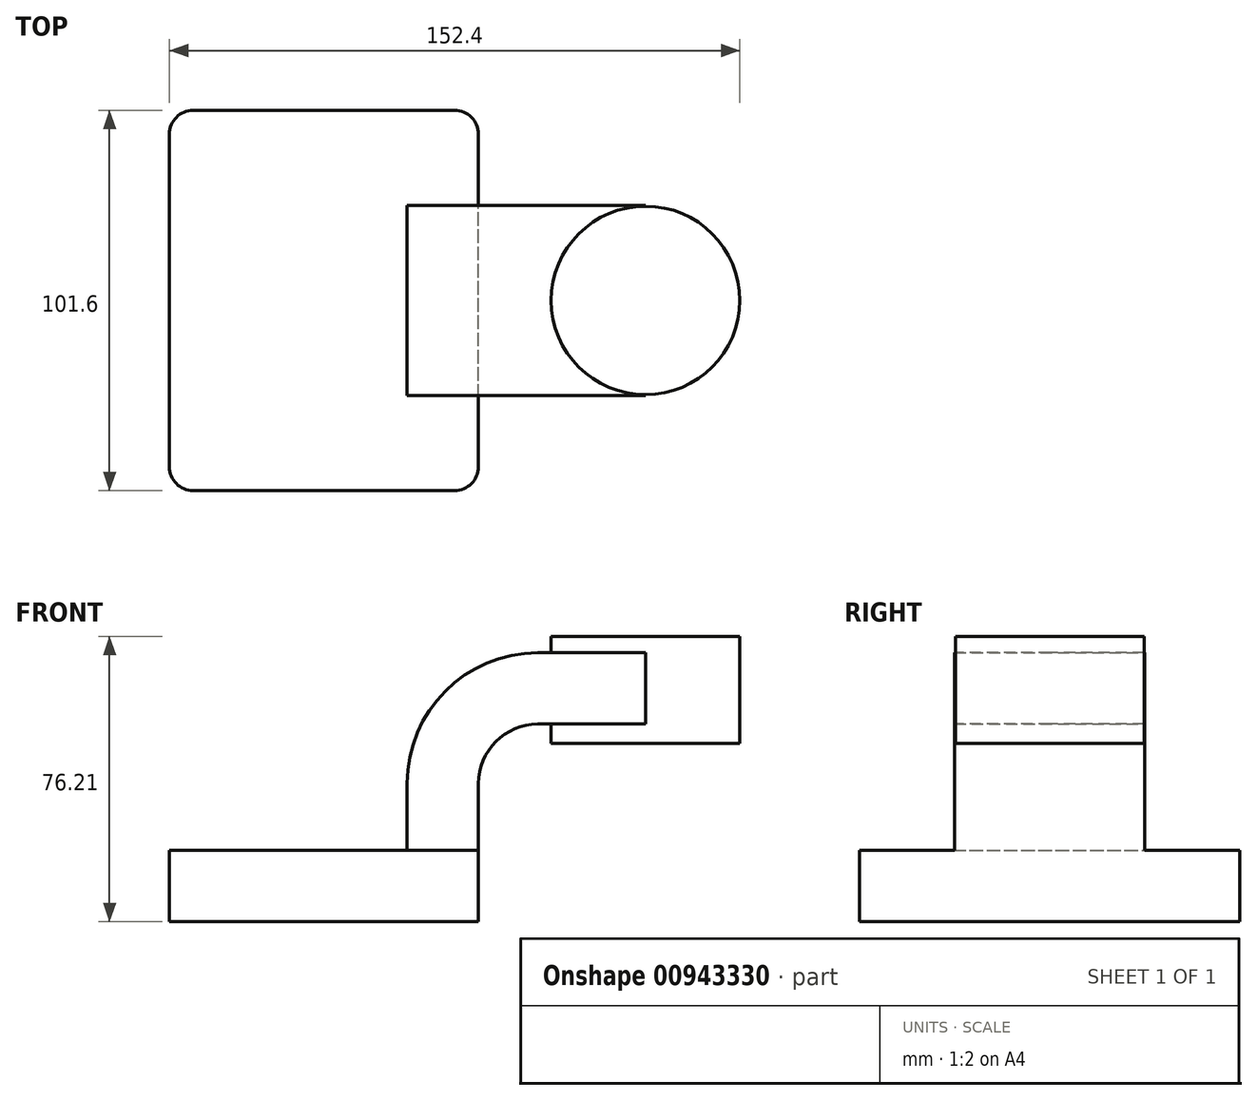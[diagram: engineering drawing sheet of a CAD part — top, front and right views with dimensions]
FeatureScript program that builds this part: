
annotation { "Feature Type Name" : "Feature", "Feature Type Description" : "" }
export const myFeature = defineFeature(function(context is Context, id is Id, definition is map)
    precondition{}
    {
        {
            var Q0;
            Q0=qCreatedBy(makeId("Front.planeOp"),FACE);
            var sketch = newSketch(context, id + "F0", { "sketchPlane" : qUnion([Q0])});
            skLineSegment(sketch, "E0.bottom", {"start": v(-41.28, 9.52) * mm, "end": v(41.27, 9.53) * mm});
            skLineSegment(sketch, "E0.top", {"start": v(-41.28, -9.53) * mm, "end": v(41.28, -9.53) * mm});
            skLineSegment(sketch, "E0.left", {"start": v(-41.28, 9.52) * mm, "end": v(-41.27, -9.53) * mm});
            skLineSegment(sketch, "E0.right", {"start": v(41.28, 9.53) * mm, "end": v(41.28, -9.52) * mm});
            skPoint(sketch, "E0.middle", {"position": v(0, 0) * mm});
            skLineSegment(sketch, "E1.bottom", {"start": v(111.12, 38.1) * mm, "end": v(60.33, 38.1) * mm});
            skLineSegment(sketch, "E1.top", {"start": v(111.13, 66.68) * mm, "end": v(60.33, 66.67) * mm});
            skLineSegment(sketch, "E1.left", {"start": v(111.13, 38.1) * mm, "end": v(111.13, 66.67) * mm});
            skLineSegment(sketch, "E1.right", {"start": v(60.33, 38.1) * mm, "end": v(60.33, 66.67) * mm});
            skPoint(sketch, "E1.middle", {"position": v(85.73, 52.39) * mm});
            skLineSegment(sketch, "E2", {"start": v(41.27, 9.53) * mm, "end": v(41.27, 27.38) * mm});
            skArc(sketch, "E3", {"start": v(41.27, 27.38) * mm, "mid": v(45.92, 38.6) * mm, "end": v(57.15, 43.26) * mm});
            skLineSegment(sketch, "E4", {"start": v(57.15, 43.26) * mm, "end": v(85.93, 43.26) * mm});
            skLineSegment(sketch, "E5.0", {"start": v(57.15, 62.3) * mm, "end": v(85.93, 62.3) * mm});
            skArc(sketch, "E5.1", {"start": v(22.22, 27.38) * mm, "mid": v(32.45, 52.08) * mm, "end": v(57.15, 62.3) * mm});
            skLineSegment(sketch, "E5.2", {"start": v(22.22, 9.53) * mm, "end": v(22.22, 27.38) * mm});
            skLineSegment(sketch, "E6", {"start": v(85.93, 38.1) * mm, "end": v(85.93, 66.68) * mm});
            skPoint(sketch, "E6.startSnap0", {"position": v(85.73, 38.1) * mm});
            skFitSpline(sketch, "E7", {"points": [v(-41.28, 9.53) * mm, v(57.15, 62.3) * mm], "startDerivative": vector(7.3, 50.65) * mm, "endDerivative": vector(195.47, 0.14) * mm});
            skSolve(sketch);
        }
        {
            var Q0;
            Q0=makeQuery(id+"F0.imprint","IMPRINT",FACE,{"disambiguationData":[TD([[makeQuery(id+"F0.imprint","IMPRINT",EDGE,{"derivedFrom":sQuery(id+"F0.wireOp",EDGE,"E0.top")}),1.0]])]});
            extrude(context, id + "F1", {"entities" : qUnion([Q0]), "endBound" : BoundingType.SYMMETRIC, "depth" : 101.6 * mm, "offsetDistance" : 25.4 * mm});
        }
        {
            var Q0;
            {var subQ5=sQuery(id+"F0.wireOp",EDGE,"E2");Q0=makeQuery(id+"F0.imprint","IMPRINT",FACE,{"disambiguationData":[TD([[makeQuery(id+"F0.imprint","IMPRINT",EDGE,{"derivedFrom":subQ5}),1.0]])]});}
            var Q1;
            {var subQ0=sQuery(id+"F0.wireOp",EDGE,"E4");var subQ1=sQuery(id+"F0.wireOp",EDGE,"E1.right");var subQ2=makeQuery(id+"F0.imprint","INTERSECT",VERTEX,{"derivedFrom":[subQ1,subQ0]});Q1=makeQuery(id+"F0.imprint","IMPRINT",FACE,{"disambiguationData":[TD([[makeQuery(id+"F0.imprint","IMPRINT",EDGE,{"disambiguationData":[TD([[subQ2,-1.0]])],"derivedFrom":subQ1}),-1.0]])]});}
            extrude(context, id + "F2", {"entities" : qUnion([Q0, Q1]), "operationType" : NewBodyOperationType.ADD, "endBound" : BoundingType.SYMMETRIC, "depth" : 50.8 * mm, "offsetDistance" : 25.4 * mm});
        }
        {
            var Q0;
            {var subQ4=sQuery(id+"F0.wireOp",EDGE,"E5.1");Q0=makeQuery(id+"F0.imprint","IMPRINT",FACE,{"disambiguationData":[TD([[makeQuery(id+"F0.imprint","IMPRINT",EDGE,{"derivedFrom":subQ4}),1.0]])]});}
            extrude(context, id + "F3", {"entities" : qUnion([Q0]), "operationType" : NewBodyOperationType.ADD, "endBound" : BoundingType.SYMMETRIC, "depth" : 15.88 * mm, "offsetDistance" : 25.4 * mm});
        }
        {
            var Q0;
            {var subQ4=sQuery(id+"F0.wireOp",EDGE,"E1.left");Q0=makeQuery(id+"F0.imprint","IMPRINT",FACE,{"disambiguationData":[TD([[makeQuery(id+"F0.imprint","IMPRINT",EDGE,{"derivedFrom":subQ4}),1.0]])]});}
            var Q1;
            Q1=sQuery(id+"F0.wireOp",EDGE,"E6");
            revolve(context, id + "F4", {"operationType" : NewBodyOperationType.ADD, "surfaceOperationType" : NewSurfaceOperationType.NEW, "entities" : qUnion([Q0]), "axis" : qUnion([Q1]), "revolveType" : RevolveType.FULL});
        }
        {
            var Q0;
            Q0=makeQuery(id+"F1.opExtrude","CAP_EDGE",EDGE,{"disambiguationData":[OSD([sQuery(id+"F0.wireOp",EDGE,"E0.right")])],"isStart":false});
            var Q1;
            Q1=makeQuery(id+"F1.opExtrude","CAP_EDGE",EDGE,{"disambiguationData":[OSD([sQuery(id+"F0.wireOp",EDGE,"E0.left")])],"isStart":false});
            var Q2;
            Q2=makeQuery(id+"F1.opExtrude","CAP_EDGE",EDGE,{"disambiguationData":[OSD([sQuery(id+"F0.wireOp",EDGE,"E0.right")])],"isStart":true});
            var Q3;
            Q3=makeQuery(id+"F1.opExtrude","CAP_EDGE",EDGE,{"disambiguationData":[OSD([sQuery(id+"F0.wireOp",EDGE,"E0.left")])],"isStart":true});
            fillet(context, id + "F5", {"entities" : qUnion([Q0, Q1, Q2, Q3]), "radius" : 6.35 * mm, "tangentPropagation" : true, "allowEdgeOverflow" : false});
        }
    });
